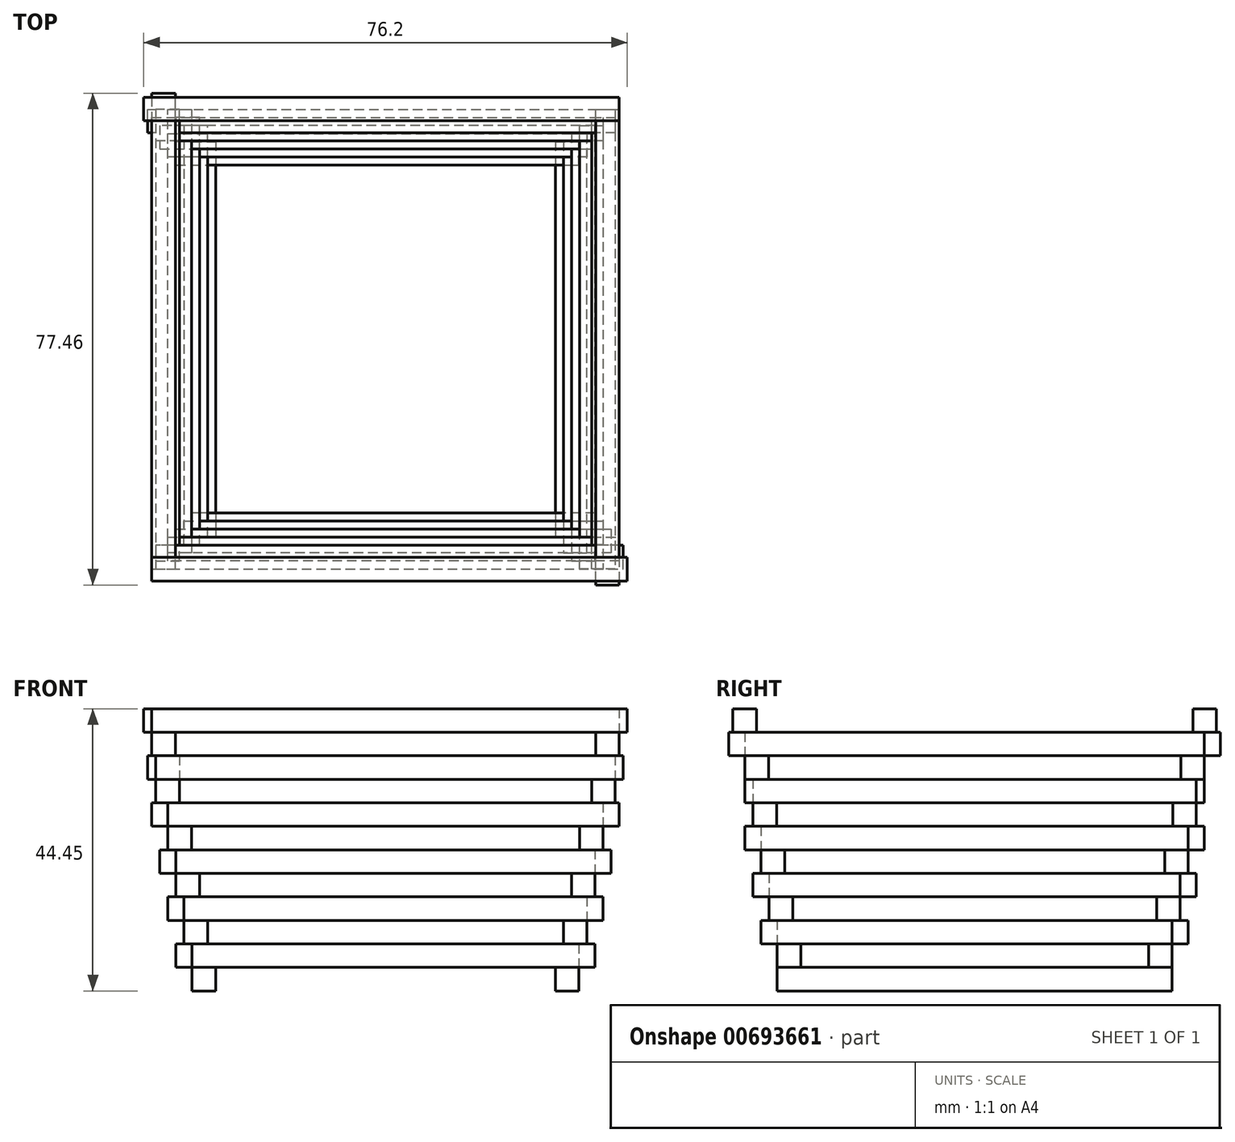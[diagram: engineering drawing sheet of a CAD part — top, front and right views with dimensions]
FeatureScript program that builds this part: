
annotation { "Feature Type Name" : "Feature", "Feature Type Description" : "" }
export const myFeature = defineFeature(function(context is Context, id is Id, definition is map)
    precondition{}
    {
        {
            var Q0;
            Q0=qCreatedBy(makeId("Top.planeOp"),FACE);
            var sketch = newSketch(context, id + "F0", { "sketchPlane" : qUnion([Q0])});
            skLineSegment(sketch, "E0.left", {"start": v(-26.78, 6.98) * mm, "end": v(-26.78, -34.82) * mm});
            skLineSegment(sketch, "E0.right", {"start": v(26.78, 34.82) * mm, "end": v(26.78, -6.98) * mm});
            skPoint(sketch, "E0.middle", {"position": v(0, 0) * mm});
            skLineSegment(sketch, "E1.bottom", {"start": v(-30.48, 31.12) * mm, "end": v(-26.78, 31.12) * mm});
            skLineSegment(sketch, "E1.top", {"start": v(-30.48, -31.12) * mm, "end": v(-26.78, -31.12) * mm});
            skLineSegment(sketch, "E1.left", {"start": v(-30.48, 31.12) * mm, "end": v(-30.48, -31.12) * mm});
            skLineSegment(sketch, "E1.right", {"start": v(30.48, 31.12) * mm, "end": v(30.48, -31.12) * mm});
            skLineSegment(sketch, "E2", {"start": v(-26.78, 6.98) * mm, "end": v(-26.78, 31.12) * mm});
            skLineSegment(sketch, "E3", {"start": v(-26.78, -31.12) * mm, "end": v(-26.78, -34.82) * mm});
            skLineSegment(sketch, "E4", {"start": v(26.78, 31.12) * mm, "end": v(26.78, 34.82) * mm});
            skLineSegment(sketch, "E5", {"start": v(26.78, -6.98) * mm, "end": v(26.78, -31.12) * mm});
            skLineSegment(sketch, "E6.trimOffspring", {"start": v(26.78, 31.12) * mm, "end": v(30.48, 31.12) * mm});
            skLineSegment(sketch, "E7.trimOffspring", {"start": v(26.78, -31.12) * mm, "end": v(30.48, -31.11) * mm});
            skSolve(sketch);
        }
        {
            var Q0;
            Q0=makeQuery(id+"F0.imprint","IMPRINT",FACE,{"disambiguationData":[TD([[makeQuery(id+"F0.imprint","IMPRINT",EDGE,{"derivedFrom":sQuery(id+"F0.wireOp",EDGE,"E0.right")}),1.0]])]});
            var Q1;
            Q1=makeQuery(id+"F0.imprint","IMPRINT",FACE,{"disambiguationData":[TD([[makeQuery(id+"F0.imprint","IMPRINT",EDGE,{"derivedFrom":sQuery(id+"F0.wireOp",EDGE,"E0.left")}),-1.0]])]});
            extrude(context, id + "F1", {"entities" : qUnion([Q0, Q1]), "depth" : 3.7 * mm, "offsetDistance" : 25.4 * mm});
        }
        {
            var Q0;
            Q0=makeQuery(id+"F1.opExtrude","CAP_FACE",FACE,{"disambiguationData":[OSD([sQuery(id+"F0.wireOp",EDGE,"E0.left"),sQuery(id+"F0.wireOp",EDGE,"E1.bottom"),sQuery(id+"F0.wireOp",EDGE,"E1.top"),sQuery(id+"F0.wireOp",EDGE,"E1.left"),sQuery(id+"F0.wireOp",EDGE,"E2"),sQuery(id+"F0.wireOp",EDGE,"E3")])],"isStart":false});
            var sketch = newSketch(context, id + "F2", { "sketchPlane" : qUnion([Q0])});
            skLineSegment(sketch, "E8", {"start": v(-30.48, -31.12) * mm, "end": v(33.02, -31.11) * mm});
            skLineSegment(sketch, "E9", {"start": v(33.02, -31.11) * mm, "end": v(33.02, -27.41) * mm});
            skLineSegment(sketch, "E10", {"start": v(33.02, -27.41) * mm, "end": v(-30.48, -27.41) * mm});
            skLineSegment(sketch, "E11", {"start": v(-30.48, -27.41) * mm, "end": v(-30.48, -31.12) * mm});
            skLineSegment(sketch, "E12", {"start": v(-33.02, 27.41) * mm, "end": v(30.48, 27.41) * mm});
            skLineSegment(sketch, "E13", {"start": v(30.48, 27.41) * mm, "end": v(30.48, 31.12) * mm});
            skLineSegment(sketch, "E14", {"start": v(30.48, 31.12) * mm, "end": v(-33.02, 31.11) * mm});
            skLineSegment(sketch, "E15", {"start": v(-33.02, 31.11) * mm, "end": v(-33.02, 27.41) * mm});
            skLineSegment(sketch, "E16", {"start": v(0, 0) * mm, "end": v(0, -27.41) * mm});
            skLineSegment(sketch, "E17", {"start": v(0, 0) * mm, "end": v(0, 27.41) * mm});
            skSolve(sketch);
        }
        {
            var Q0;
            {var subQ1=sQuery(id+"F2.wireOp",EDGE,"E13");Q0=makeQuery(id+"F2.imprint","IMPRINT",FACE,{"disambiguationData":[TD([[makeQuery(id+"F2.imprint","IMPRINT",EDGE,{"derivedFrom":subQ1}),1.0]])]});}
            var Q1;
            {var subQ0=sQuery(id+"F2.wireOp",EDGE,"E15");Q1=makeQuery(id+"F2.imprint","IMPRINT",FACE,{"disambiguationData":[TD([[makeQuery(id+"F2.imprint","IMPRINT",EDGE,{"derivedFrom":subQ0}),1.0]])]});}
            var Q2;
            {var subQ0=sQuery(id+"F2.wireOp",EDGE,"E12");var subQ1=makeQuery(id+"F1.opExtrude","CAP_EDGE",EDGE,{"disambiguationData":[OSD([sQuery(id+"F0.wireOp",EDGE,"E1.left")])],"isStart":false});var subQ2=makeQuery(id+"F2.imprint","INTERSECT",VERTEX,{"derivedFrom":[subQ1,subQ0]});Q2=makeQuery(id+"F2.imprint","IMPRINT",FACE,{"disambiguationData":[TD([[makeQuery(id+"F2.imprint","IMPRINT",EDGE,{"disambiguationData":[TD([[subQ2,1.0]])],"derivedFrom":subQ1}),1.0]])]});}
            var Q3;
            {var subQ5=sQuery(id+"F2.wireOp",EDGE,"E8");Q3=makeQuery(id+"F2.imprint","IMPRINT",FACE,{"disambiguationData":[TD([[makeQuery(id+"F2.imprint","IMPRINT",EDGE,{"derivedFrom":subQ5}),1.0]])]});}
            var Q4;
            {var subQ0=sQuery(id+"F2.wireOp",EDGE,"E11");var subQ1=sQuery(id+"F2.wireOp",EDGE,"E10");var subQ2=makeQuery(id+"F2.imprint","INTERSECT",VERTEX,{"derivedFrom":[subQ1,subQ0]});Q4=makeQuery(id+"F2.imprint","IMPRINT",FACE,{"disambiguationData":[TD([[makeQuery(id+"F2.imprint","IMPRINT",EDGE,{"disambiguationData":[TD([[subQ2,-1.0]])],"derivedFrom":subQ0}),1.0]])]});}
            var Q5;
            {var subQ6=sQuery(id+"F2.wireOp",EDGE,"E9");Q5=makeQuery(id+"F2.imprint","IMPRINT",FACE,{"disambiguationData":[TD([[makeQuery(id+"F2.imprint","IMPRINT",EDGE,{"derivedFrom":subQ6}),1.0]])]});}
            extrude(context, id + "F3", {"entities" : qUnion([Q0, Q1, Q2, Q3, Q4, Q5]), "depth" : 3.7 * mm, "offsetDistance" : 25.4 * mm});
        }
        {
            var Q0;
            Q0=makeQuery(id+"F3.opExtrude","CAP_FACE",FACE,{"disambiguationData":[OSD([sQuery(id+"F2.wireOp",EDGE,"E12"),sQuery(id+"F2.wireOp",EDGE,"E13"),sQuery(id+"F2.wireOp",EDGE,"E14"),sQuery(id+"F2.wireOp",EDGE,"E15")])],"isStart":false});
            var sketch = newSketch(context, id + "F4", { "sketchPlane" : qUnion([Q0])});
            skLineSegment(sketch, "E18", {"start": v(-31.75, 33.66) * mm, "end": v(-31.75, -31.12) * mm});
            skLineSegment(sketch, "E19", {"start": v(-31.75, -31.12) * mm, "end": v(-28.05, -31.12) * mm});
            skLineSegment(sketch, "E20", {"start": v(-28.05, -31.12) * mm, "end": v(-28.05, 33.66) * mm});
            skLineSegment(sketch, "E21", {"start": v(-28.05, 33.66) * mm, "end": v(-31.75, 33.66) * mm});
            skLineSegment(sketch, "E22", {"start": v(28.05, 31.12) * mm, "end": v(28.05, -33.65) * mm});
            skLineSegment(sketch, "E23", {"start": v(28.05, -33.65) * mm, "end": v(31.75, -33.65) * mm});
            skLineSegment(sketch, "E24", {"start": v(31.75, -33.65) * mm, "end": v(31.75, 31.12) * mm});
            skLineSegment(sketch, "E25", {"start": v(31.75, 31.12) * mm, "end": v(28.05, 31.12) * mm});
            skLineSegment(sketch, "E26", {"start": v(-28.05, 0) * mm, "end": v(28.05, 0) * mm});
            skSolve(sketch);
        }
        {
            var Q0;
            {var subQ4=sQuery(id+"F4.wireOp",EDGE,"E19");Q0=makeQuery(id+"F4.imprint","IMPRINT",FACE,{"disambiguationData":[TD([[makeQuery(id+"F4.imprint","IMPRINT",EDGE,{"derivedFrom":subQ4}),1.0]])]});}
            var Q1;
            {var subQ0=sQuery(id+"F4.wireOp",EDGE,"E21");Q1=makeQuery(id+"F4.imprint","IMPRINT",FACE,{"disambiguationData":[TD([[makeQuery(id+"F4.imprint","IMPRINT",EDGE,{"derivedFrom":subQ0}),1.0]])]});}
            var Q2;
            {var subQ0=sQuery(id+"F4.wireOp",EDGE,"E18");var subQ1=makeQuery(id+"F3.opExtrude","CAP_EDGE",EDGE,{"disambiguationData":[OSD([sQuery(id+"F2.wireOp",EDGE,"E14")])],"isStart":false});var subQ2=makeQuery(id+"F4.imprint","INTERSECT",VERTEX,{"derivedFrom":[subQ1,subQ0]});Q2=makeQuery(id+"F4.imprint","IMPRINT",FACE,{"disambiguationData":[TD([[makeQuery(id+"F4.imprint","IMPRINT",EDGE,{"disambiguationData":[TD([[subQ2,-1.0]])],"derivedFrom":subQ0}),1.0]])]});}
            var Q3;
            {var subQ5=makeQuery(id+"F3.opExtrude","CAP_EDGE",EDGE,{"disambiguationData":[OSD([sQuery(id+"F2.wireOp",EDGE,"E13")])],"isStart":false});Q3=makeQuery(id+"F4.imprint","IMPRINT",FACE,{"disambiguationData":[TD([[makeQuery(id+"F4.imprint","IMPRINT",EDGE,{"derivedFrom":subQ5}),1.0]])]});}
            var Q4;
            {var subQ1=sQuery(id+"F4.wireOp",EDGE,"E23");Q4=makeQuery(id+"F4.imprint","IMPRINT",FACE,{"disambiguationData":[TD([[makeQuery(id+"F4.imprint","IMPRINT",EDGE,{"derivedFrom":subQ1}),1.0]])]});}
            extrude(context, id + "F5", {"entities" : qUnion([Q0, Q1, Q2, Q3, Q4]), "depth" : 3.7 * mm, "offsetDistance" : 25.4 * mm});
        }
        {
            var Q0;
            Q0=makeQuery(id+"F5.opExtrude","CAP_FACE",FACE,{"disambiguationData":[OSD([sQuery(id+"F4.wireOp",EDGE,"E18"),sQuery(id+"F4.wireOp",EDGE,"E19"),sQuery(id+"F4.wireOp",EDGE,"E20"),sQuery(id+"F4.wireOp",EDGE,"E21")])],"isStart":false});
            var sketch = newSketch(context, id + "F6", { "sketchPlane" : qUnion([Q0])});
            skLineSegment(sketch, "E27", {"start": v(-34.3, 32.38) * mm, "end": v(31.75, 32.39) * mm});
            skLineSegment(sketch, "E28", {"start": v(31.75, 32.39) * mm, "end": v(31.75, 28.68) * mm});
            skLineSegment(sketch, "E29", {"start": v(31.75, 28.68) * mm, "end": v(-34.3, 28.68) * mm});
            skLineSegment(sketch, "E30", {"start": v(-34.3, 28.68) * mm, "end": v(-34.3, 32.38) * mm});
            skLineSegment(sketch, "E31", {"start": v(-31.75, -28.68) * mm, "end": v(34.3, -28.68) * mm});
            skLineSegment(sketch, "E32", {"start": v(34.3, -28.68) * mm, "end": v(34.3, -32.38) * mm});
            skLineSegment(sketch, "E33", {"start": v(34.3, -32.38) * mm, "end": v(-31.75, -32.39) * mm});
            skLineSegment(sketch, "E34", {"start": v(-31.75, -32.39) * mm, "end": v(-31.75, -28.68) * mm});
            skLineSegment(sketch, "E35", {"start": v(0, 28.68) * mm, "end": v(0, -28.68) * mm});
            skSolve(sketch);
        }
        {
            var Q0;
            {var subQ1=sQuery(id+"F6.wireOp",EDGE,"E32");Q0=makeQuery(id+"F6.imprint","IMPRINT",FACE,{"disambiguationData":[TD([[makeQuery(id+"F6.imprint","IMPRINT",EDGE,{"derivedFrom":subQ1}),-1.0]])]});}
            var Q1;
            {var subQ5=makeQuery(id+"F5.opExtrude","CAP_EDGE",EDGE,{"disambiguationData":[OSD([sQuery(id+"F4.wireOp",EDGE,"E19")])],"isStart":false});Q1=makeQuery(id+"F6.imprint","IMPRINT",FACE,{"disambiguationData":[TD([[makeQuery(id+"F6.imprint","IMPRINT",EDGE,{"derivedFrom":subQ5}),1.0]])]});}
            var Q2;
            {var subQ4=sQuery(id+"F6.wireOp",EDGE,"E28");Q2=makeQuery(id+"F6.imprint","IMPRINT",FACE,{"disambiguationData":[TD([[makeQuery(id+"F6.imprint","IMPRINT",EDGE,{"derivedFrom":subQ4}),-1.0]])]});}
            var Q3;
            {var subQ0=sQuery(id+"F6.wireOp",EDGE,"E27");var subQ1=makeQuery(id+"F5.opExtrude","CAP_EDGE",EDGE,{"disambiguationData":[OSD([sQuery(id+"F4.wireOp",EDGE,"E18")])],"isStart":false});var subQ2=makeQuery(id+"F6.imprint","INTERSECT",VERTEX,{"derivedFrom":[subQ1,subQ0]});Q3=makeQuery(id+"F6.imprint","IMPRINT",FACE,{"disambiguationData":[TD([[makeQuery(id+"F6.imprint","IMPRINT",EDGE,{"disambiguationData":[TD([[subQ2,-1.0]])],"derivedFrom":subQ0}),-1.0]])]});}
            var Q4;
            {var subQ0=sQuery(id+"F6.wireOp",EDGE,"E30");Q4=makeQuery(id+"F6.imprint","IMPRINT",FACE,{"disambiguationData":[TD([[makeQuery(id+"F6.imprint","IMPRINT",EDGE,{"derivedFrom":subQ0}),-1.0]])]});}
            extrude(context, id + "F7", {"entities" : qUnion([Q0, Q1, Q2, Q3, Q4]), "depth" : 3.7 * mm, "offsetDistance" : 25.4 * mm});
        }
        {
            var Q0;
            Q0=makeQuery(id+"F7.opExtrude","CAP_FACE",FACE,{"disambiguationData":[OSD([sQuery(id+"F6.wireOp",EDGE,"E27"),sQuery(id+"F6.wireOp",EDGE,"E28"),sQuery(id+"F6.wireOp",EDGE,"E29"),sQuery(id+"F6.wireOp",EDGE,"E30")])],"isStart":false});
            var sketch = newSketch(context, id + "F8", { "sketchPlane" : qUnion([Q0])});
            skLineSegment(sketch, "E36", {"start": v(33.02, -34.93) * mm, "end": v(33.02, 32.39) * mm});
            skLineSegment(sketch, "E37", {"start": v(33.02, 32.39) * mm, "end": v(29.32, 32.39) * mm});
            skLineSegment(sketch, "E38", {"start": v(29.32, 32.39) * mm, "end": v(29.32, -34.93) * mm});
            skLineSegment(sketch, "E39", {"start": v(29.32, -34.93) * mm, "end": v(33.02, -34.93) * mm});
            skLineSegment(sketch, "E40", {"start": v(-29.32, -32.39) * mm, "end": v(-29.32, 34.93) * mm});
            skLineSegment(sketch, "E41", {"start": v(-29.32, 34.93) * mm, "end": v(-33.02, 34.93) * mm});
            skLineSegment(sketch, "E42", {"start": v(-33.02, 34.93) * mm, "end": v(-33.02, -32.39) * mm});
            skLineSegment(sketch, "E43", {"start": v(-33.02, -32.39) * mm, "end": v(-29.32, -32.39) * mm});
            skLineSegment(sketch, "E44", {"start": v(29.32, 0) * mm, "end": v(-29.32, 0) * mm});
            skSolve(sketch);
        }
        {
            var Q0;
            {var subQ0=sQuery(id+"F8.wireOp",EDGE,"E43");Q0=makeQuery(id+"F8.imprint","IMPRINT",FACE,{"disambiguationData":[TD([[makeQuery(id+"F8.imprint","IMPRINT",EDGE,{"derivedFrom":subQ0}),1.0]])]});}
            var Q1;
            {var subQ0=sQuery(id+"F8.wireOp",EDGE,"E41");Q1=makeQuery(id+"F8.imprint","IMPRINT",FACE,{"disambiguationData":[TD([[makeQuery(id+"F8.imprint","IMPRINT",EDGE,{"derivedFrom":subQ0}),1.0]])]});}
            var Q2;
            {var subQ0=sQuery(id+"F8.wireOp",EDGE,"E40");var subQ1=makeQuery(id+"F7.opExtrude","CAP_EDGE",EDGE,{"disambiguationData":[OSD([sQuery(id+"F6.wireOp",EDGE,"E27")])],"isStart":false});var subQ2=makeQuery(id+"F8.imprint","INTERSECT",VERTEX,{"derivedFrom":[subQ1,subQ0]});Q2=makeQuery(id+"F8.imprint","IMPRINT",FACE,{"disambiguationData":[TD([[makeQuery(id+"F8.imprint","IMPRINT",EDGE,{"disambiguationData":[TD([[subQ2,1.0]])],"derivedFrom":subQ0}),1.0]])]});}
            var Q3;
            {var subQ1=makeQuery(id+"F7.opExtrude","CAP_EDGE",EDGE,{"disambiguationData":[OSD([sQuery(id+"F6.wireOp",EDGE,"E28")])],"isStart":false});Q3=makeQuery(id+"F8.imprint","IMPRINT",FACE,{"disambiguationData":[TD([[makeQuery(id+"F8.imprint","IMPRINT",EDGE,{"derivedFrom":subQ1}),-1.0]])]});}
            var Q4;
            {var subQ6=sQuery(id+"F8.wireOp",EDGE,"E36");Q4=makeQuery(id+"F8.imprint","IMPRINT",FACE,{"disambiguationData":[TD([[makeQuery(id+"F8.imprint","IMPRINT",EDGE,{"derivedFrom":subQ6}),1.0]])]});}
            extrude(context, id + "F9", {"entities" : qUnion([Q0, Q1, Q2, Q3, Q4]), "depth" : 3.7 * mm, "offsetDistance" : 25.4 * mm});
        }
        {
            var Q0;
            Q0=makeQuery(id+"F9.opExtrude","CAP_FACE",FACE,{"disambiguationData":[OSD([sQuery(id+"F8.wireOp",EDGE,"E40"),sQuery(id+"F8.wireOp",EDGE,"E41"),sQuery(id+"F8.wireOp",EDGE,"E42"),sQuery(id+"F8.wireOp",EDGE,"E43")])],"isStart":false});
            var sketch = newSketch(context, id + "F10", { "sketchPlane" : qUnion([Q0])});
            skLineSegment(sketch, "E45", {"start": v(-33.02, -29.95) * mm, "end": v(35.56, -29.95) * mm});
            skLineSegment(sketch, "E46", {"start": v(35.56, -29.95) * mm, "end": v(35.56, -33.65) * mm});
            skLineSegment(sketch, "E47", {"start": v(35.56, -33.65) * mm, "end": v(-33.02, -33.66) * mm});
            skLineSegment(sketch, "E48", {"start": v(-33.02, -33.66) * mm, "end": v(-33.02, -29.95) * mm});
            skLineSegment(sketch, "E49", {"start": v(-35.56, 29.95) * mm, "end": v(33.02, 29.95) * mm});
            skLineSegment(sketch, "E50", {"start": v(33.02, 29.95) * mm, "end": v(33.02, 33.66) * mm});
            skLineSegment(sketch, "E51", {"start": v(33.02, 33.66) * mm, "end": v(-35.56, 33.65) * mm});
            skLineSegment(sketch, "E52", {"start": v(-35.56, 33.65) * mm, "end": v(-35.56, 29.95) * mm});
            skLineSegment(sketch, "E53", {"start": v(0, 29.95) * mm, "end": v(0, -29.95) * mm});
            skSolve(sketch);
        }
        {
            var Q0;
            {var subQ1=sQuery(id+"F10.wireOp",EDGE,"E50");Q0=makeQuery(id+"F10.imprint","IMPRINT",FACE,{"disambiguationData":[TD([[makeQuery(id+"F10.imprint","IMPRINT",EDGE,{"derivedFrom":subQ1}),1.0]])]});}
            var Q1;
            {var subQ0=sQuery(id+"F10.wireOp",EDGE,"E49");var subQ1=makeQuery(id+"F9.opExtrude","CAP_EDGE",EDGE,{"disambiguationData":[OSD([sQuery(id+"F8.wireOp",EDGE,"E42")])],"isStart":false});var subQ2=makeQuery(id+"F10.imprint","INTERSECT",VERTEX,{"derivedFrom":[subQ1,subQ0]});Q1=makeQuery(id+"F10.imprint","IMPRINT",FACE,{"disambiguationData":[TD([[makeQuery(id+"F10.imprint","IMPRINT",EDGE,{"disambiguationData":[TD([[subQ2,-1.0]])],"derivedFrom":subQ0}),1.0]])]});}
            var Q2;
            {var subQ0=sQuery(id+"F10.wireOp",EDGE,"E52");Q2=makeQuery(id+"F10.imprint","IMPRINT",FACE,{"disambiguationData":[TD([[makeQuery(id+"F10.imprint","IMPRINT",EDGE,{"derivedFrom":subQ0}),1.0]])]});}
            var Q3;
            {var subQ5=makeQuery(id+"F9.opExtrude","CAP_EDGE",EDGE,{"disambiguationData":[OSD([sQuery(id+"F8.wireOp",EDGE,"E43")])],"isStart":false});Q3=makeQuery(id+"F10.imprint","IMPRINT",FACE,{"disambiguationData":[TD([[makeQuery(id+"F10.imprint","IMPRINT",EDGE,{"derivedFrom":subQ5}),1.0]])]});}
            var Q4;
            {var subQ1=sQuery(id+"F10.wireOp",EDGE,"E46");Q4=makeQuery(id+"F10.imprint","IMPRINT",FACE,{"disambiguationData":[TD([[makeQuery(id+"F10.imprint","IMPRINT",EDGE,{"derivedFrom":subQ1}),-1.0]])]});}
            extrude(context, id + "F11", {"entities" : qUnion([Q0, Q1, Q2, Q3, Q4]), "depth" : 3.7 * mm, "offsetDistance" : 25.4 * mm});
        }
        {
            var Q0;
            Q0=makeQuery(id+"F11.opExtrude","CAP_FACE",FACE,{"disambiguationData":[OSD([sQuery(id+"F10.wireOp",EDGE,"E49"),sQuery(id+"F10.wireOp",EDGE,"E50"),sQuery(id+"F10.wireOp",EDGE,"E51"),sQuery(id+"F10.wireOp",EDGE,"E52")])],"isStart":false});
            var sketch = newSketch(context, id + "F12", { "sketchPlane" : qUnion([Q0])});
            skLineSegment(sketch, "E54", {"start": v(34.29, 33.66) * mm, "end": v(34.3, -36.2) * mm});
            skLineSegment(sketch, "E55", {"start": v(34.3, -36.2) * mm, "end": v(30.59, -36.2) * mm});
            skLineSegment(sketch, "E56", {"start": v(30.59, -36.2) * mm, "end": v(30.59, 33.66) * mm});
            skLineSegment(sketch, "E57", {"start": v(30.59, 33.66) * mm, "end": v(34.29, 33.66) * mm});
            skLineSegment(sketch, "E58", {"start": v(-30.59, 36.2) * mm, "end": v(-30.59, -33.66) * mm});
            skLineSegment(sketch, "E59", {"start": v(-30.59, -33.66) * mm, "end": v(-34.29, -33.66) * mm});
            skLineSegment(sketch, "E60", {"start": v(-34.3, -33.66) * mm, "end": v(-34.3, 36.2) * mm});
            skLineSegment(sketch, "E61", {"start": v(-34.3, 36.2) * mm, "end": v(-30.59, 36.2) * mm});
            skLineSegment(sketch, "E62", {"start": v(30.59, 0) * mm, "end": v(-30.59, 0) * mm});
            skSolve(sketch);
        }
        {
            var Q0;
            {var subQ1=sQuery(id+"F12.wireOp",EDGE,"E59");Q0=makeQuery(id+"F12.imprint","IMPRINT",FACE,{"disambiguationData":[TD([[makeQuery(id+"F12.imprint","IMPRINT",EDGE,{"derivedFrom":subQ1}),-1.0]])]});}
            var Q1;
            {var subQ0=sQuery(id+"F12.wireOp",EDGE,"E58");var subQ1=makeQuery(id+"F11.opExtrude","CAP_EDGE",EDGE,{"disambiguationData":[OSD([sQuery(id+"F10.wireOp",EDGE,"E51")])],"isStart":false});var subQ2=makeQuery(id+"F12.imprint","INTERSECT",VERTEX,{"derivedFrom":[subQ1,subQ0]});Q1=makeQuery(id+"F12.imprint","IMPRINT",FACE,{"disambiguationData":[TD([[makeQuery(id+"F12.imprint","IMPRINT",EDGE,{"disambiguationData":[TD([[subQ2,-1.0]])],"derivedFrom":subQ0}),-1.0]])]});}
            var Q2;
            {var subQ0=sQuery(id+"F12.wireOp",EDGE,"E61");Q2=makeQuery(id+"F12.imprint","IMPRINT",FACE,{"disambiguationData":[TD([[makeQuery(id+"F12.imprint","IMPRINT",EDGE,{"derivedFrom":subQ0}),-1.0]])]});}
            var Q3;
            {var subQ5=sQuery(id+"F12.wireOp",EDGE,"E54");Q3=makeQuery(id+"F12.imprint","IMPRINT",FACE,{"disambiguationData":[TD([[makeQuery(id+"F12.imprint","IMPRINT",EDGE,{"derivedFrom":subQ5}),-1.0]])]});}
            var Q4;
            {var subQ5=makeQuery(id+"F11.opExtrude","CAP_EDGE",EDGE,{"disambiguationData":[OSD([sQuery(id+"F10.wireOp",EDGE,"E50")])],"isStart":false});Q4=makeQuery(id+"F12.imprint","IMPRINT",FACE,{"disambiguationData":[TD([[makeQuery(id+"F12.imprint","IMPRINT",EDGE,{"derivedFrom":subQ5}),1.0]])]});}
            extrude(context, id + "F13", {"entities" : qUnion([Q0, Q1, Q2, Q3, Q4]), "depth" : 3.7 * mm, "offsetDistance" : 25.4 * mm});
        }
        {
            var Q0;
            Q0=makeQuery(id+"F13.opExtrude","CAP_FACE",FACE,{"disambiguationData":[OSD([sQuery(id+"F12.wireOp",EDGE,"E58"),sQuery(id+"F12.wireOp",EDGE,"E59"),sQuery(id+"F12.wireOp",EDGE,"E60"),sQuery(id+"F12.wireOp",EDGE,"E61")])],"isStart":false});
            var sketch = newSketch(context, id + "F14", { "sketchPlane" : qUnion([Q0])});
            skLineSegment(sketch, "E63", {"start": v(-36.83, 34.92) * mm, "end": v(34.29, 34.93) * mm});
            skLineSegment(sketch, "E64", {"start": v(34.29, 34.93) * mm, "end": v(34.29, 31.22) * mm});
            skLineSegment(sketch, "E65", {"start": v(34.29, 31.22) * mm, "end": v(-36.83, 31.22) * mm});
            skLineSegment(sketch, "E66", {"start": v(-36.83, 31.22) * mm, "end": v(-36.83, 34.92) * mm});
            skLineSegment(sketch, "E67", {"start": v(-34.3, -31.22) * mm, "end": v(36.83, -31.22) * mm});
            skLineSegment(sketch, "E68", {"start": v(36.83, -31.22) * mm, "end": v(36.83, -34.92) * mm});
            skLineSegment(sketch, "E69", {"start": v(36.83, -34.92) * mm, "end": v(-34.29, -34.93) * mm});
            skLineSegment(sketch, "E70", {"start": v(-34.29, -34.93) * mm, "end": v(-34.29, -31.22) * mm});
            skLineSegment(sketch, "E71", {"start": v(0, 31.22) * mm, "end": v(0, -31.22) * mm});
            skSolve(sketch);
        }
        {
            var Q0;
            {var subQ4=sQuery(id+"F14.wireOp",EDGE,"E64");Q0=makeQuery(id+"F14.imprint","IMPRINT",FACE,{"disambiguationData":[TD([[makeQuery(id+"F14.imprint","IMPRINT",EDGE,{"derivedFrom":subQ4}),-1.0]])]});}
            var Q1;
            {var subQ0=sQuery(id+"F14.wireOp",EDGE,"E63");var subQ1=makeQuery(id+"F13.opExtrude","CAP_EDGE",EDGE,{"disambiguationData":[OSD([sQuery(id+"F12.wireOp",EDGE,"E60")])],"isStart":false});var subQ2=makeQuery(id+"F14.imprint","INTERSECT",VERTEX,{"derivedFrom":[subQ1,subQ0]});Q1=makeQuery(id+"F14.imprint","IMPRINT",FACE,{"disambiguationData":[TD([[makeQuery(id+"F14.imprint","IMPRINT",EDGE,{"disambiguationData":[TD([[subQ2,-1.0]])],"derivedFrom":subQ0}),-1.0]])]});}
            var Q2;
            {var subQ0=sQuery(id+"F14.wireOp",EDGE,"E66");Q2=makeQuery(id+"F14.imprint","IMPRINT",FACE,{"disambiguationData":[TD([[makeQuery(id+"F14.imprint","IMPRINT",EDGE,{"derivedFrom":subQ0}),-1.0]])]});}
            var Q3;
            {var subQ5=makeQuery(id+"F13.opExtrude","CAP_EDGE",EDGE,{"disambiguationData":[OSD([sQuery(id+"F12.wireOp",EDGE,"E59")])],"isStart":false});Q3=makeQuery(id+"F14.imprint","IMPRINT",FACE,{"disambiguationData":[TD([[makeQuery(id+"F14.imprint","IMPRINT",EDGE,{"derivedFrom":subQ5}),-1.0]])]});}
            var Q4;
            {var subQ1=sQuery(id+"F14.wireOp",EDGE,"E68");Q4=makeQuery(id+"F14.imprint","IMPRINT",FACE,{"disambiguationData":[TD([[makeQuery(id+"F14.imprint","IMPRINT",EDGE,{"derivedFrom":subQ1}),-1.0]])]});}
            extrude(context, id + "F15", {"entities" : qUnion([Q0, Q1, Q2, Q3, Q4]), "depth" : 3.7 * mm, "offsetDistance" : 25.4 * mm});
        }
        {
            var Q0;
            Q0=makeQuery(id+"F15.opExtrude","CAP_FACE",FACE,{"disambiguationData":[OSD([sQuery(id+"F14.wireOp",EDGE,"E63"),sQuery(id+"F14.wireOp",EDGE,"E64"),sQuery(id+"F14.wireOp",EDGE,"E65"),sQuery(id+"F14.wireOp",EDGE,"E66")])],"isStart":false});
            var sketch = newSketch(context, id + "F16", { "sketchPlane" : qUnion([Q0])});
            skLineSegment(sketch, "E72", {"start": v(36.2, 34.93) * mm, "end": v(36.2, -36.2) * mm});
            skLineSegment(sketch, "E73", {"start": v(36.2, -36.2) * mm, "end": v(32.5, -36.2) * mm});
            skLineSegment(sketch, "E74", {"start": v(32.5, -36.2) * mm, "end": v(32.5, 34.93) * mm});
            skLineSegment(sketch, "E75", {"start": v(32.5, 34.93) * mm, "end": v(36.2, 34.93) * mm});
            skLineSegment(sketch, "E76", {"start": v(-32.5, 36.2) * mm, "end": v(-36.2, 36.2) * mm});
            skLineSegment(sketch, "E77", {"start": v(-36.2, 36.2) * mm, "end": v(-36.2, -34.93) * mm});
            skLineSegment(sketch, "E78", {"start": v(-36.2, -34.93) * mm, "end": v(-32.5, -34.93) * mm});
            skLineSegment(sketch, "E79", {"start": v(-32.5, -34.93) * mm, "end": v(-32.5, 36.2) * mm});
            skLineSegment(sketch, "E80", {"start": v(32.5, 0) * mm, "end": v(-32.5, 0) * mm});
            skSolve(sketch);
        }
        {
            var Q0;
            {var subQ6=sQuery(id+"F16.wireOp",EDGE,"E78");Q0=makeQuery(id+"F16.imprint","IMPRINT",FACE,{"disambiguationData":[TD([[makeQuery(id+"F16.imprint","IMPRINT",EDGE,{"derivedFrom":subQ6}),1.0]])]});}
            var Q1;
            {var subQ0=sQuery(id+"F16.wireOp",EDGE,"E77");var subQ1=makeQuery(id+"F15.opExtrude","CAP_EDGE",EDGE,{"disambiguationData":[OSD([sQuery(id+"F14.wireOp",EDGE,"E63")])],"isStart":false});var subQ2=makeQuery(id+"F16.imprint","INTERSECT",VERTEX,{"derivedFrom":[subQ1,subQ0]});Q1=makeQuery(id+"F16.imprint","IMPRINT",FACE,{"disambiguationData":[TD([[makeQuery(id+"F16.imprint","IMPRINT",EDGE,{"disambiguationData":[TD([[subQ2,-1.0]])],"derivedFrom":subQ0}),1.0]])]});}
            var Q2;
            {var subQ0=sQuery(id+"F16.wireOp",EDGE,"E76");Q2=makeQuery(id+"F16.imprint","IMPRINT",FACE,{"disambiguationData":[TD([[makeQuery(id+"F16.imprint","IMPRINT",EDGE,{"derivedFrom":subQ0}),1.0]])]});}
            var Q3;
            {var subQ5=makeQuery(id+"F15.opExtrude","CAP_EDGE",EDGE,{"disambiguationData":[OSD([sQuery(id+"F14.wireOp",EDGE,"E64")])],"isStart":false});Q3=makeQuery(id+"F16.imprint","IMPRINT",FACE,{"disambiguationData":[TD([[makeQuery(id+"F16.imprint","IMPRINT",EDGE,{"derivedFrom":subQ5}),-1.0]])]});}
            var Q4;
            {var subQ6=sQuery(id+"F16.wireOp",EDGE,"E72");Q4=makeQuery(id+"F16.imprint","IMPRINT",FACE,{"disambiguationData":[TD([[makeQuery(id+"F16.imprint","IMPRINT",EDGE,{"derivedFrom":subQ6}),-1.0]])]});}
            extrude(context, id + "F17", {"entities" : qUnion([Q0, Q1, Q2, Q3, Q4]), "depth" : 3.7 * mm, "offsetDistance" : 25.4 * mm});
        }
        {
            var Q0;
            Q0=makeQuery(id+"F17.opExtrude","CAP_FACE",FACE,{"disambiguationData":[OSD([sQuery(id+"F16.wireOp",EDGE,"E76"),sQuery(id+"F16.wireOp",EDGE,"E77"),sQuery(id+"F16.wireOp",EDGE,"E78"),sQuery(id+"F16.wireOp",EDGE,"E79")])],"isStart":false});
            var sketch = newSketch(context, id + "F18", { "sketchPlane" : qUnion([Q0])});
            skLineSegment(sketch, "E81", {"start": v(-37.46, 36.2) * mm, "end": v(36.2, 36.2) * mm});
            skLineSegment(sketch, "E82", {"start": v(36.2, 36.2) * mm, "end": v(36.2, 32.5) * mm});
            skLineSegment(sketch, "E83", {"start": v(36.2, 32.5) * mm, "end": v(-37.46, 32.5) * mm});
            skLineSegment(sketch, "E84", {"start": v(-37.46, 32.5) * mm, "end": v(-37.46, 36.2) * mm});
            skLineSegment(sketch, "E85", {"start": v(-36.2, -32.5) * mm, "end": v(-36.2, -36.2) * mm});
            skLineSegment(sketch, "E86", {"start": v(-36.2, -36.2) * mm, "end": v(37.47, -36.2) * mm});
            skLineSegment(sketch, "E87", {"start": v(37.47, -36.2) * mm, "end": v(37.47, -32.5) * mm});
            skLineSegment(sketch, "E88", {"start": v(37.46, -32.5) * mm, "end": v(-36.2, -32.5) * mm});
            skLineSegment(sketch, "E89", {"start": v(0, 32.5) * mm, "end": v(0, -32.5) * mm});
            skSolve(sketch);
        }
        {
            var Q0;
            {var subQ4=sQuery(id+"F18.wireOp",EDGE,"E82");Q0=makeQuery(id+"F18.imprint","IMPRINT",FACE,{"disambiguationData":[TD([[makeQuery(id+"F18.imprint","IMPRINT",EDGE,{"derivedFrom":subQ4}),-1.0]])]});}
            var Q1;
            {var subQ0=sQuery(id+"F18.wireOp",EDGE,"E81");var subQ1=makeQuery(id+"F17.opExtrude","CAP_EDGE",EDGE,{"disambiguationData":[OSD([sQuery(id+"F16.wireOp",EDGE,"E77")])],"isStart":false});var subQ2=makeQuery(id+"F18.imprint","INTERSECT",VERTEX,{"derivedFrom":[subQ1,subQ0]});Q1=makeQuery(id+"F18.imprint","IMPRINT",FACE,{"disambiguationData":[TD([[makeQuery(id+"F18.imprint","IMPRINT",EDGE,{"disambiguationData":[TD([[subQ2,-1.0]])],"derivedFrom":subQ0}),-1.0]])]});}
            var Q2;
            {var subQ0=sQuery(id+"F18.wireOp",EDGE,"E84");Q2=makeQuery(id+"F18.imprint","IMPRINT",FACE,{"disambiguationData":[TD([[makeQuery(id+"F18.imprint","IMPRINT",EDGE,{"derivedFrom":subQ0}),-1.0]])]});}
            var Q3;
            {var subQ1=makeQuery(id+"F17.opExtrude","CAP_EDGE",EDGE,{"disambiguationData":[OSD([sQuery(id+"F16.wireOp",EDGE,"E78")])],"isStart":false});Q3=makeQuery(id+"F18.imprint","IMPRINT",FACE,{"disambiguationData":[TD([[makeQuery(id+"F18.imprint","IMPRINT",EDGE,{"derivedFrom":subQ1}),1.0]])]});}
            var Q4;
            {var subQ6=sQuery(id+"F18.wireOp",EDGE,"E86");Q4=makeQuery(id+"F18.imprint","IMPRINT",FACE,{"disambiguationData":[TD([[makeQuery(id+"F18.imprint","IMPRINT",EDGE,{"derivedFrom":subQ6}),1.0]])]});}
            extrude(context, id + "F19", {"entities" : qUnion([Q0, Q1, Q2, Q3, Q4]), "depth" : 3.7 * mm, "offsetDistance" : 25.4 * mm});
        }
        {
            var Q0;
            Q0=makeQuery(id+"F19.opExtrude","CAP_FACE",FACE,{"disambiguationData":[OSD([sQuery(id+"F18.wireOp",EDGE,"E81"),sQuery(id+"F18.wireOp",EDGE,"E82"),sQuery(id+"F18.wireOp",EDGE,"E83"),sQuery(id+"F18.wireOp",EDGE,"E84")])],"isStart":false});
            var sketch = newSketch(context, id + "F20", { "sketchPlane" : qUnion([Q0])});
            skLineSegment(sketch, "E90", {"start": v(36.83, 36.2) * mm, "end": v(36.83, -38.73) * mm});
            skLineSegment(sketch, "E91", {"start": v(36.83, -38.73) * mm, "end": v(33.13, -38.73) * mm});
            skLineSegment(sketch, "E92", {"start": v(33.13, -38.73) * mm, "end": v(33.13, 36.2) * mm});
            skLineSegment(sketch, "E93", {"start": v(33.13, 36.2) * mm, "end": v(36.83, 36.2) * mm});
            skLineSegment(sketch, "E94", {"start": v(-33.13, 38.73) * mm, "end": v(-36.83, 38.73) * mm});
            skLineSegment(sketch, "E95", {"start": v(-36.83, 38.73) * mm, "end": v(-36.83, -36.2) * mm});
            skLineSegment(sketch, "E96", {"start": v(-36.83, -36.2) * mm, "end": v(-33.13, -36.2) * mm});
            skLineSegment(sketch, "E97", {"start": v(-33.13, -36.2) * mm, "end": v(-33.13, 38.73) * mm});
            skLineSegment(sketch, "E98", {"start": v(33.13, 0) * mm, "end": v(-33.13, 0) * mm});
            skSolve(sketch);
        }
        {
            var Q0;
            {var subQ6=sQuery(id+"F20.wireOp",EDGE,"E96");Q0=makeQuery(id+"F20.imprint","IMPRINT",FACE,{"disambiguationData":[TD([[makeQuery(id+"F20.imprint","IMPRINT",EDGE,{"derivedFrom":subQ6}),1.0]])]});}
            var Q1;
            {var subQ0=sQuery(id+"F20.wireOp",EDGE,"E95");var subQ1=makeQuery(id+"F19.opExtrude","CAP_EDGE",EDGE,{"disambiguationData":[OSD([sQuery(id+"F18.wireOp",EDGE,"E81")])],"isStart":false});var subQ2=makeQuery(id+"F20.imprint","INTERSECT",VERTEX,{"derivedFrom":[subQ1,subQ0]});Q1=makeQuery(id+"F20.imprint","IMPRINT",FACE,{"disambiguationData":[TD([[makeQuery(id+"F20.imprint","IMPRINT",EDGE,{"disambiguationData":[TD([[subQ2,-1.0]])],"derivedFrom":subQ0}),1.0]])]});}
            var Q2;
            {var subQ0=sQuery(id+"F20.wireOp",EDGE,"E94");Q2=makeQuery(id+"F20.imprint","IMPRINT",FACE,{"disambiguationData":[TD([[makeQuery(id+"F20.imprint","IMPRINT",EDGE,{"derivedFrom":subQ0}),1.0]])]});}
            var Q3;
            {var subQ6=sQuery(id+"F20.wireOp",EDGE,"E90");Q3=makeQuery(id+"F20.imprint","IMPRINT",FACE,{"disambiguationData":[TD([[makeQuery(id+"F20.imprint","IMPRINT",EDGE,{"derivedFrom":subQ6}),-1.0]])]});}
            var Q4;
            {var subQ5=makeQuery(id+"F19.opExtrude","CAP_EDGE",EDGE,{"disambiguationData":[OSD([sQuery(id+"F18.wireOp",EDGE,"E82")])],"isStart":false});Q4=makeQuery(id+"F20.imprint","IMPRINT",FACE,{"disambiguationData":[TD([[makeQuery(id+"F20.imprint","IMPRINT",EDGE,{"derivedFrom":subQ5}),-1.0]])]});}
            extrude(context, id + "F21", {"entities" : qUnion([Q0, Q1, Q2, Q3, Q4]), "depth" : 3.7 * mm, "offsetDistance" : 25.4 * mm});
        }
        {
            var Q0;
            Q0=makeQuery(id+"F21.opExtrude","CAP_FACE",FACE,{"disambiguationData":[OSD([sQuery(id+"F20.wireOp",EDGE,"E94"),sQuery(id+"F20.wireOp",EDGE,"E95"),sQuery(id+"F20.wireOp",EDGE,"E96"),sQuery(id+"F20.wireOp",EDGE,"E97")])],"isStart":false});
            var sketch = newSketch(context, id + "F22", { "sketchPlane" : qUnion([Q0])});
            skLineSegment(sketch, "E99", {"start": v(-38.1, 34.4) * mm, "end": v(36.83, 34.4) * mm});
            skLineSegment(sketch, "E100", {"start": v(36.83, 34.4) * mm, "end": v(36.83, 38.1) * mm});
            skLineSegment(sketch, "E101", {"start": v(36.83, 38.1) * mm, "end": v(-38.1, 38.1) * mm});
            skLineSegment(sketch, "E102", {"start": v(-38.1, 38.1) * mm, "end": v(-38.1, 34.4) * mm});
            skLineSegment(sketch, "E103", {"start": v(-36.83, -34.4) * mm, "end": v(-36.83, -38.1) * mm});
            skLineSegment(sketch, "E104", {"start": v(-36.83, -38.1) * mm, "end": v(38.1, -38.1) * mm});
            skLineSegment(sketch, "E105", {"start": v(38.1, -38.1) * mm, "end": v(38.1, -34.4) * mm});
            skLineSegment(sketch, "E106", {"start": v(38.1, -34.4) * mm, "end": v(-36.83, -34.4) * mm});
            skLineSegment(sketch, "E107", {"start": v(0, 34.4) * mm, "end": v(0, -34.4) * mm});
            skSolve(sketch);
        }
        {
            var Q0;
            {var subQ1=sQuery(id+"F22.wireOp",EDGE,"E100");Q0=makeQuery(id+"F22.imprint","IMPRINT",FACE,{"disambiguationData":[TD([[makeQuery(id+"F22.imprint","IMPRINT",EDGE,{"derivedFrom":subQ1}),1.0]])]});}
            var Q1;
            {var subQ0=sQuery(id+"F22.wireOp",EDGE,"E102");Q1=makeQuery(id+"F22.imprint","IMPRINT",FACE,{"disambiguationData":[TD([[makeQuery(id+"F22.imprint","IMPRINT",EDGE,{"derivedFrom":subQ0}),1.0]])]});}
            var Q2;
            {var subQ0=sQuery(id+"F22.wireOp",EDGE,"E99");var subQ1=makeQuery(id+"F21.opExtrude","CAP_EDGE",EDGE,{"disambiguationData":[OSD([sQuery(id+"F20.wireOp",EDGE,"E95")])],"isStart":false});var subQ2=makeQuery(id+"F22.imprint","INTERSECT",VERTEX,{"derivedFrom":[subQ1,subQ0]});Q2=makeQuery(id+"F22.imprint","IMPRINT",FACE,{"disambiguationData":[TD([[makeQuery(id+"F22.imprint","IMPRINT",EDGE,{"disambiguationData":[TD([[subQ2,-1.0]])],"derivedFrom":subQ0}),1.0]])]});}
            var Q3;
            {var subQ1=makeQuery(id+"F21.opExtrude","CAP_EDGE",EDGE,{"disambiguationData":[OSD([sQuery(id+"F20.wireOp",EDGE,"E96")])],"isStart":false});Q3=makeQuery(id+"F22.imprint","IMPRINT",FACE,{"disambiguationData":[TD([[makeQuery(id+"F22.imprint","IMPRINT",EDGE,{"derivedFrom":subQ1}),1.0]])]});}
            var Q4;
            {var subQ6=sQuery(id+"F22.wireOp",EDGE,"E104");Q4=makeQuery(id+"F22.imprint","IMPRINT",FACE,{"disambiguationData":[TD([[makeQuery(id+"F22.imprint","IMPRINT",EDGE,{"derivedFrom":subQ6}),1.0]])]});}
            extrude(context, id + "F23", {"entities" : qUnion([Q0, Q1, Q2, Q3, Q4]), "depth" : 3.7 * mm, "offsetDistance" : 25.4 * mm});
        }
    });
